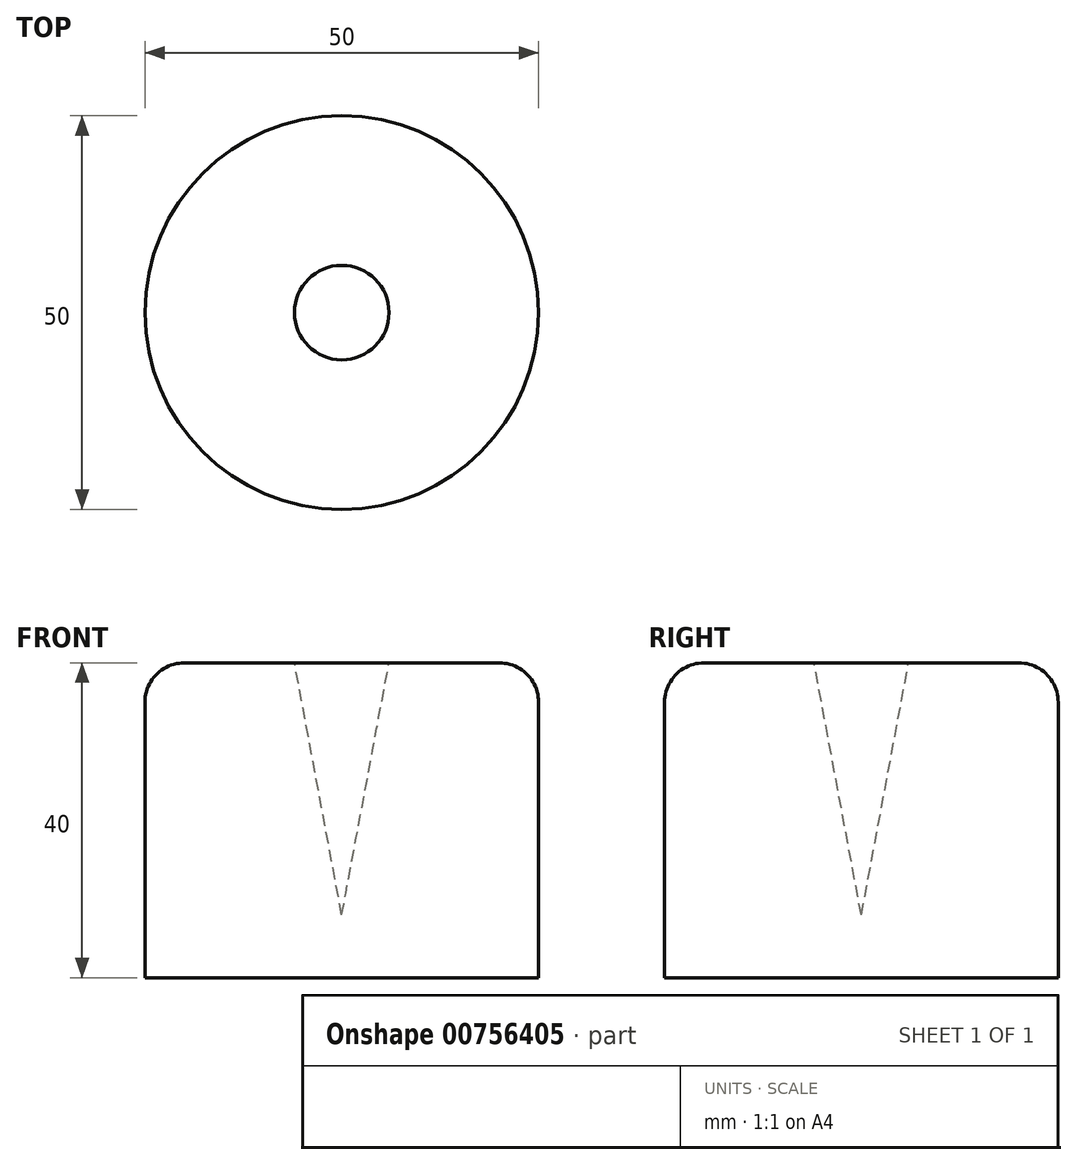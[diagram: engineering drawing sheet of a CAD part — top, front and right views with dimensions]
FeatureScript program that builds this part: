
annotation { "Feature Type Name" : "Feature", "Feature Type Description" : "" }
export const myFeature = defineFeature(function(context is Context, id is Id, definition is map)
    precondition{}
    {
        {
            var Q0;
            Q0=qCreatedBy(makeId("Top.planeOp"),FACE);
            var sketch = newSketch(context, id + "F0", { "sketchPlane" : qUnion([Q0])});
            skCircle(sketch, "E0", {"center": v(0, 0) * mm, "radius": 25 * mm});
            skSolve(sketch);
        }
        {
            var Q0;
            Q0 = qSketchRegion(id + "F0", true);
            extrude(context, id + "F1", {"entities" : qUnion([Q0]), "depth" : 40 * mm, "offsetDistance" : 25 * mm});
        }
        {
            var Q0;
            Q0=makeQuery(id+"F1.opExtrude","CAP_FACE",FACE,{"disambiguationData":[OSD([sQuery(id+"F0.wireOp",EDGE,"E0")])],"isStart":false});
            var sketch = newSketch(context, id + "F2", { "sketchPlane" : qUnion([Q0])});
            skPoint(sketch, "E1", {"position": v(0, 0) * mm});
            skPoint(sketch, "E2", {"position": v(1.62, 24.95) * mm});
            skCircle(sketch, "E3", {"center": v(0, 0) * mm, "radius": 6 * mm});
            skSolve(sketch);
        }
        {
            var Q0;
            Q0=sQuery(id+"F2.wireOp",VERTEX,"E1");
            var Q1;
            Q1=sQuery(id+"F2.wireOp",VERTEX,"E2");
            var Q2;
            Q2=qCreatedBy(makeId("Origin.pointOp"),VERTEX);
            cPlane(context, id + "F3", {"entities" : qUnion([Q0, Q1, Q2]), "cplaneType" : CPlaneType.THREE_POINT, "offset" : 25 * mm, "width" : 150 * mm, "height" : 150 * mm});
        }
        {
            var Q0;
            Q0=qCreatedBy(id+"F3.planeOp",FACE);
            var sketch = newSketch(context, id + "F4", { "sketchPlane" : qUnion([Q0])});
            skPoint(sketch, "E4", {"position": v(0, 40) * mm});
            skPoint(sketch, "E5", {"position": v(25, 40) * mm});
            skLineSegment(sketch, "E6", {"start": v(0, 40) * mm, "end": v(0, 8) * mm});
            skLineSegment(sketch, "E7", {"start": v(0, 40) * mm, "end": v(6, 40) * mm});
            skLineSegment(sketch, "E8", {"start": v(6, 40) * mm, "end": v(0, 8) * mm});
            skSolve(sketch);
        }
        {
            var Q0;
            Q0 = qSketchRegion(id + "F4", true);
            var Q1;
            Q1=sQuery(id+"F4.wireOp",EDGE,"E6");
            revolve(context, id + "F5", {"operationType" : NewBodyOperationType.REMOVE, "surfaceOperationType" : NewSurfaceOperationType.NEW, "entities" : qUnion([Q0]), "axis" : qUnion([Q1]), "revolveType" : RevolveType.FULL, "oppositeDirection" : true});
        }
        {
            var Q0;
            Q0=makeQuery(id+"F1.opExtrude","CAP_EDGE",EDGE,{"disambiguationData":[OSD([sQuery(id+"F0.wireOp",EDGE,"E0")])],"isStart":false});
            fillet(context, id + "F6", {"entities" : qUnion([Q0]), "radius" : 5 * mm, "tangentPropagation" : true, "allowEdgeOverflow" : false});
        }
    });
